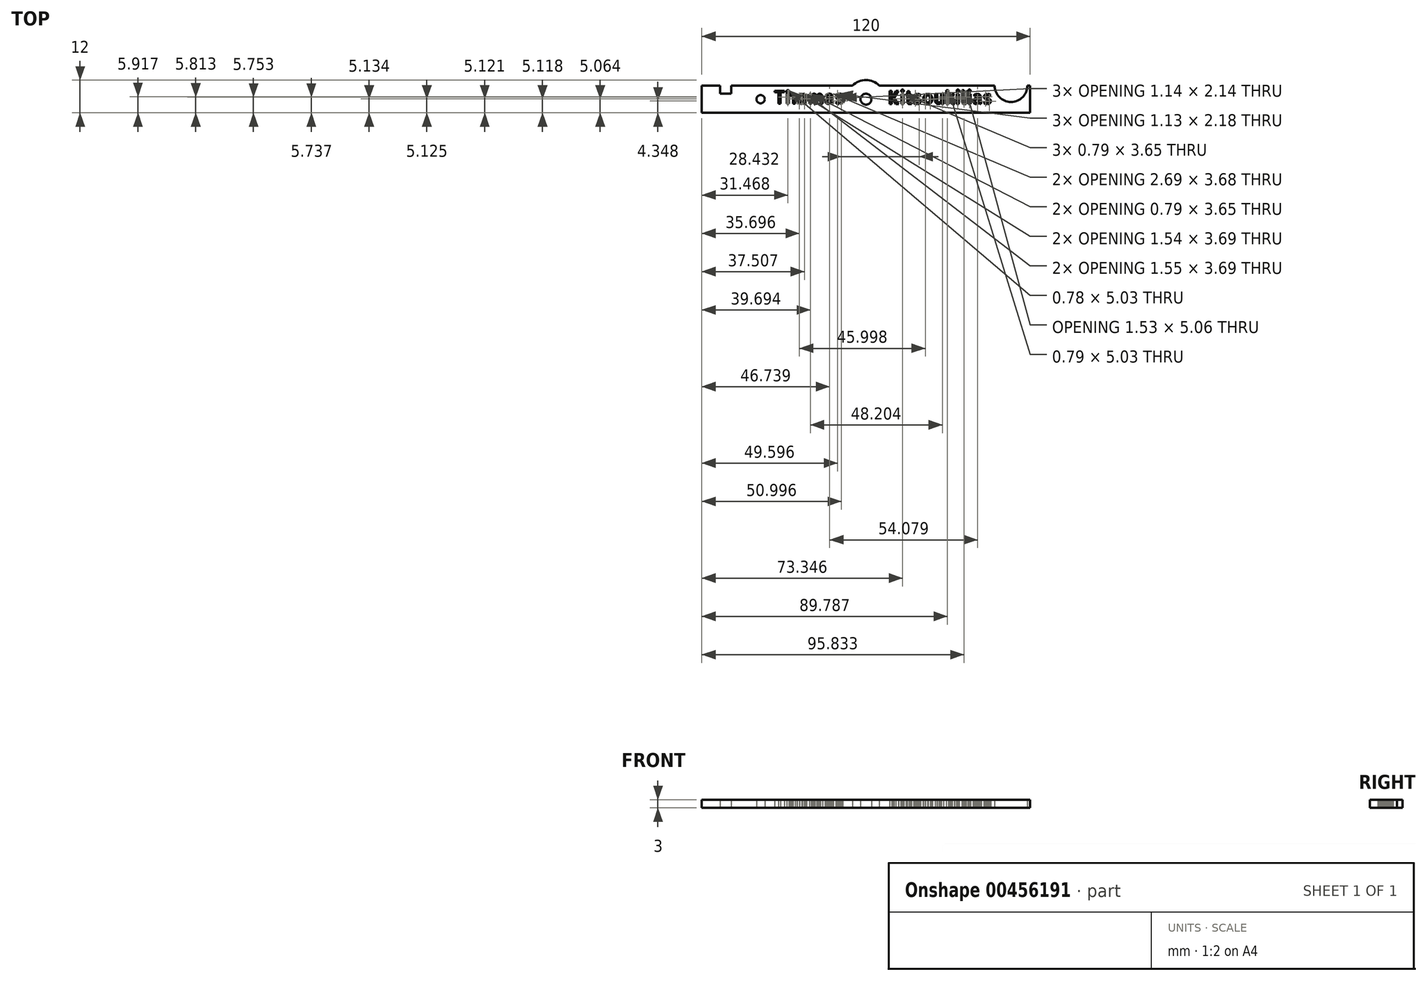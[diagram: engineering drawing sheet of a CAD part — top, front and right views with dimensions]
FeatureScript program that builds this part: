
annotation { "Feature Type Name" : "Feature", "Feature Type Description" : "" }
export const myFeature = defineFeature(function(context is Context, id is Id, definition is map)
    precondition{}
    {
        {
            var Q0;
            Q0=qCreatedBy(makeId("Top.planeOp"),FACE);
            var sketch = newSketch(context, id + "F0", { "sketchPlane" : qUnion([Q0])});
            skLineSegment(sketch, "E0.bottom", {"start": v(-60, 5) * mm, "end": v(60, 5) * mm});
            skLineSegment(sketch, "E0.top", {"start": v(-60, -5) * mm, "end": v(60, -5) * mm});
            skLineSegment(sketch, "E0.left", {"start": v(-60, 5) * mm, "end": v(-60, -5) * mm});
            skLineSegment(sketch, "E0.right", {"start": v(60, 5) * mm, "end": v(60, -5) * mm});
            skPoint(sketch, "E0.middle", {"position": v(0, 0) * mm});
            skLineSegment(sketch, "E1.bottom", {"start": v(-53.3, 5) * mm, "end": v(-49.3, 5) * mm});
            skLineSegment(sketch, "E1.top", {"start": v(-53.3, 2) * mm, "end": v(-49.3, 2) * mm});
            skLineSegment(sketch, "E1.left", {"start": v(-53.3, 5) * mm, "end": v(-53.3, 2) * mm});
            skLineSegment(sketch, "E1.right", {"start": v(-49.3, 5) * mm, "end": v(-49.3, 2) * mm});
            skCircle(sketch, "E2", {"center": v(0, 0) * mm, "radius": 2 * mm});
            skCircle(sketch, "E3", {"center": v(0, 0) * mm, "radius": 7 * mm});
            skCircle(sketch, "E4", {"center": v(-38.5, 0) * mm, "radius": 1.5 * mm});
            skCircle(sketch, "E5", {"center": v(53, 5) * mm, "radius": 6 * mm});
            skText(sketch, "E6", { "text": "Thomas", "fontName": "AllertaStencil-Regular.ttf"});
            skText(sketch, "E7", { "text": "Kitsoukilias", "fontName": "AllertaStencil-Regular.ttf"});
            const initialGuessF0  = {"E6": [-0.03377, -0.0017, 1, 0, 0.00477], "E7": [0.00808, -0.00176, 1, 0, 0.00477]};
            skSetInitialGuess(sketch, initialGuessF0);
            skSolve(sketch);
        }
        {
            var Q0;
            {var subQ0=sQuery(id+"F0.wireOp",EDGE,"E0.left");Q0=makeQuery(id+"F0.imprint","IMPRINT",FACE,{"disambiguationData":[TD([[makeQuery(id+"F0.imprint","IMPRINT",EDGE,{"derivedFrom":subQ0}),1.0]])]});}
            var Q1;
            {var subQ0=sQuery(id+"F0.wireOp",EDGE,"E0.right");Q1=makeQuery(id+"F0.imprint","IMPRINT",FACE,{"disambiguationData":[TD([[makeQuery(id+"F0.imprint","IMPRINT",EDGE,{"derivedFrom":subQ0}),-1.0]])]});}
            var Q2;
            {var subQ0=sQuery(id+"F0.wireOp",EDGE,"E3");var subQ1=sQuery(id+"F0.wireOp",EDGE,"E0.bottom");var subQ2=makeQuery(id+"F0.imprint","INTERSECT",VERTEX,{"disambiguationData":[OD(0.0)],"derivedFrom":[subQ1,subQ0]});Q2=makeQuery(id+"F0.imprint","IMPRINT",FACE,{"disambiguationData":[TD([[makeQuery(id+"F0.imprint","IMPRINT",EDGE,{"disambiguationData":[TD([[subQ2,-1.0]])],"derivedFrom":subQ1}),1.0]])]});}
            var Q3;
            {var subQ0=sQuery(id+"F0.wireOp",EDGE,"E3");var subQ1=sQuery(id+"F0.wireOp",EDGE,"E0.top");var subQ2=makeQuery(id+"F0.imprint","INTERSECT",VERTEX,{"disambiguationData":[OD(0.0)],"derivedFrom":[subQ1,subQ0]});Q3=makeQuery(id+"F0.imprint","IMPRINT",FACE,{"disambiguationData":[TD([[makeQuery(id+"F0.imprint","IMPRINT",EDGE,{"disambiguationData":[TD([[subQ2,-1.0]])],"derivedFrom":subQ1}),-1.0]])]});}
            var Q4;
            Q4=makeQuery(id+"F0.imprint","IMPRINT",FACE,{"disambiguationData":[TD([[makeQuery(id+"F0.imprint","IMPRINT",EDGE,{"derivedFrom":sQuery(id+"F0.wireOp",EDGE,"E2")}),-1.0]])]});
            extrude(context, id + "F1", {"entities" : qUnion([Q0, Q1, Q2, Q3, Q4]), "depth" : 3 * mm});
        }
    });
